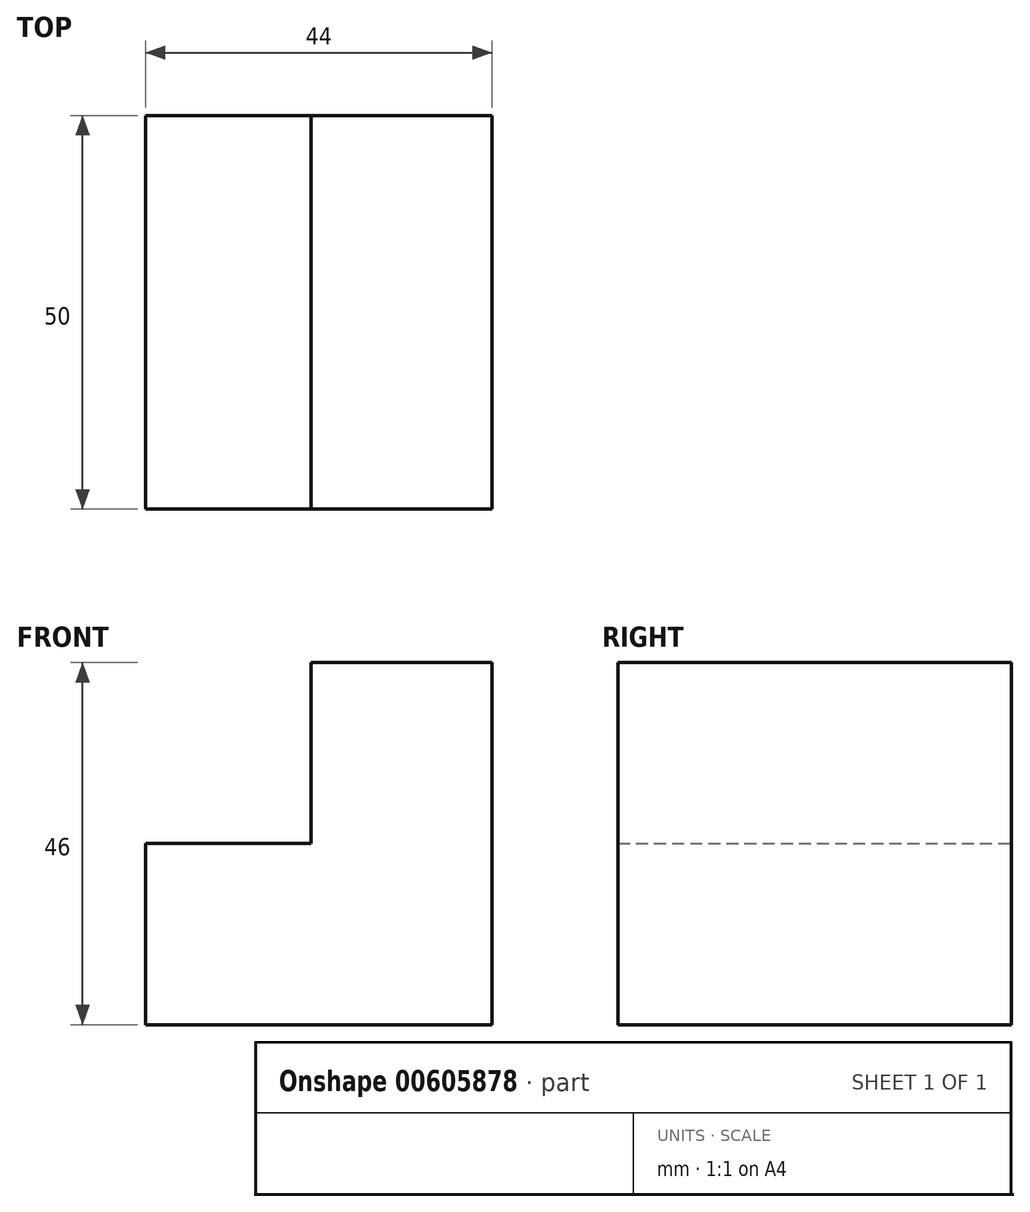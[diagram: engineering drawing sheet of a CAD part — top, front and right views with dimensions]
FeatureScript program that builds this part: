
annotation { "Feature Type Name" : "Feature", "Feature Type Description" : "" }
export const myFeature = defineFeature(function(context is Context, id is Id, definition is map)
    precondition{}
    {
        {
            var Q0;
            Q0=qCreatedBy(makeId("Front.planeOp"),FACE);
            var sketch = newSketch(context, id + "F0", { "sketchPlane" : qUnion([Q0])});
            skLineSegment(sketch, "E0", {"start": v(0, 23.4) * mm, "end": v(23, 23.4) * mm});
            skLineSegment(sketch, "E1", {"start": v(23, 23.4) * mm, "end": v(23, -22.6) * mm});
            skLineSegment(sketch, "E2", {"start": v(23, -22.6) * mm, "end": v(-21, -22.6) * mm});
            skLineSegment(sketch, "E3", {"start": v(-21, -22.6) * mm, "end": v(-21, 0.4) * mm});
            skLineSegment(sketch, "E4", {"start": v(-21, 0.4) * mm, "end": v(0, 0.4) * mm});
            skLineSegment(sketch, "E5", {"start": v(0, 23.4) * mm, "end": v(0, 0.4) * mm});
            skSolve(sketch);
        }
        {
            var Q0;
            Q0 = qSketchRegion(id + "F0", true);
            extrude(context, id + "F1", {"entities" : qUnion([Q0]), "depth" : 25 * mm, "offsetDistance" : 25 * mm});
        }
        {
            var Q0;
            Q0=qCreatedBy(makeId("Right.planeOp"),FACE);
            var sketch = newSketch(context, id + "F2", { "sketchPlane" : qUnion([Q0])});
            skLineSegment(sketch, "E6", {"start": v(0, 0) * mm, "end": v(23, 0) * mm});
            skLineSegment(sketch, "E7", {"start": v(23, 0) * mm, "end": v(23, -22.26) * mm});
            skLineSegment(sketch, "E8", {"start": v(23, -22.26) * mm, "end": v(0, -22.26) * mm});
            skLineSegment(sketch, "E9", {"start": v(0, 22.85) * mm, "end": v(23, 22.85) * mm});
            skLineSegment(sketch, "E10", {"start": v(23, 22.85) * mm, "end": v(23, 0) * mm});
            skSolve(sketch);
        }
        {
            var Q0;
            Q0 = qSketchRegion(id + "F2", true);
            var Q1;
            Q1=makeQuery(id+"F1.opExtrude","CAP_FACE",FACE,{"disambiguationData":[OSD([sQuery(id+"F0.wireOp",EDGE,"E0"),sQuery(id+"F0.wireOp",EDGE,"E1"),sQuery(id+"F0.wireOp",EDGE,"E2"),sQuery(id+"F0.wireOp",EDGE,"E3"),sQuery(id+"F0.wireOp",EDGE,"E4"),sQuery(id+"F0.wireOp",EDGE,"E5")])],"isStart":true});
            extrude(context, id + "F3", {"entities" : qUnion([Q0, Q1]), "operationType" : NewBodyOperationType.ADD, "depth" : 25 * mm, "offsetDistance" : 25 * mm});
        }
    });
